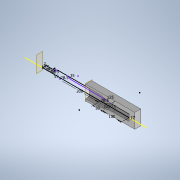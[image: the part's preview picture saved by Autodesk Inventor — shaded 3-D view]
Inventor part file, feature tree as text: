
AUTODESK INVENTOR PART (.ipt)
format: ipt  version: 2022 (Build 260153000, 153)  size: 232,960 bytes
history: native  units: mm
features: sketch x2, extrude x2, plane x2, revolve x1, fillet x1, boolean_combine x1, split x1
ambient origin geometry x8: Origin, YZ Plane, XZ Plane, XY Plane, X Axis, Y Axis, Z Axis, Center Point
bodies: Solid2 (feature_tree), Solid3 (feature_tree)
feature tree (10):
  sketch  "Sketch1"  dims[d0=41.0mm d1=6.0mm]
  revolve  "Revolution2"  [1 undecoded]
  extrude  "Extrusion2"  Depth=2.0mm
  fillet  "Fillet1"  Radius=50.0mm
  extrude  "Extrusion3"  Depth=2.0mm
  boolean_combine  "Combine1"
  plane  "Work Plane2"
  split  "Split1"
  sketch  "Sketch2"  dims[d2=59.0mm d3=200.0mm d4=50.0mm d5=100.0mm d6=19.5mm d7=19.5mm d8=28.5mm d10=28.5mm d11=17.0mm d12=17.0mm d13=2.0mm d14=8.0mm d16=125.0mm d17=125.0mm d18=2.0mm d25=35.0mm d26=28.5mm d27=180.0deg d28=100.0mm d29=0.0mm d30=2.0mm d31=516.0mm d32=77.0mm d33=31.5mm d34=0.0mm d35=-30.0mm d36=258.0mm d19=0.872665mm d20=0.872665mm]
  plane  "Work Plane1"
note: 1 required parameter value undecoded (feature->parameter linkage not recoverable at this tier; creation-order binding heuristic only, values carry confidence <= 0.55)
